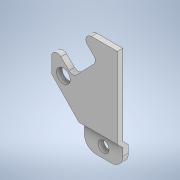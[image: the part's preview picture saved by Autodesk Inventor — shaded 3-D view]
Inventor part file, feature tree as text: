
AUTODESK INVENTOR PART (.ipt)
format: ipt  version: 2020 (Build 240168000, 168)  size: 250,880 bytes
history: native  units: mm
features: extrude x6, sketch x6, fillet x3, chamfer x2, projected_geometry x2
ambient origin geometry x8: Origin, YZ Plane, XZ Plane, XY Plane, X Axis, Y Axis, Z Axis, Center Point
bodies: Solid1 (feature_tree)
feature tree (19):
  extrude  "Extrusion1"  TaperAngle=0.0deg  [1 undecoded]
  extrude  "Extrusion5"  Depth=5.0mm
  fillet  "Fillet2"  Radius=2.5mm
  extrude  "Extrusion6"  Depth=1.0mm
  chamfer  "Chamfer1"  Distance=0.1mm
  extrude  "Extrusion7"  Depth=1.0mm
  chamfer  "Chamfer2"  [1 undecoded]
  extrude  "Extrusion8"  Depth=1.0mm
  extrude  "Extrusion9"  Depth=2.0mm
  fillet  "Fillet3"  Radius=3.525mm
  fillet  "Fillet4"  Radius=2.6mm
  sketch  "Sketch1"  dims[d6=1.0mm d7=0.0mm]
  sketch  "Sketch7"  dims[d26=4.95mm d27=7.25mm d28=2.5mm d29=4.9mm d30=14.9mm d31=5.1mm d32=5.1mm d33=90.0deg d34=135.0deg d36=0.0mm d37=0.0mm]
  projected_geometry  "Projected Loop2"
  sketch  "Sketch8"  dims[d38=2.5mm d39=5.0mm d40=2.5mm]
  sketch  "Sketch9"  dims[d41=1.0mm d42=7.5mm]
  projected_geometry  "Projected Loop3"
  sketch  "Sketch10"  dims[d43=0.15mm]
  sketch  "Sketch11"  dims[d44=0.15mm d54=0.1mm d55=0.1mm d56=0.0mm d57=4.5mm d58=2.0mm d59=3.525mm d60=2.6mm d61=2.0mm d62=0.0mm d63=5.0mm d64=45.0deg d65=5.0mm d66=45.0deg d67=2.1mm d68=0.2mm d69=0.1mm d70=10.0mm d71=0.0mm d72=1.0mm d73=2.0mm d74=45.0deg d75=1.0mm d76=0.0mm d77=1.0mm d78=2.0mm d79=45.0deg d80=3.8mm d81=1.0mm d82=0.0mm d83=7.0mm d85=6.5mm d86=3.5mm d87=1.0mm d88=0.0mm d89=6.5mm d90=1.0mm d91=1.0mm d5=0.5mm d8=0.872665mm d11=0.5mm d12=0.872665mm d13=0.5mm d14=0.872665mm d25=0.5mm]
note: 2 required parameter values undecoded (feature->parameter linkage not recoverable at this tier; creation-order binding heuristic only, values carry confidence <= 0.55)
